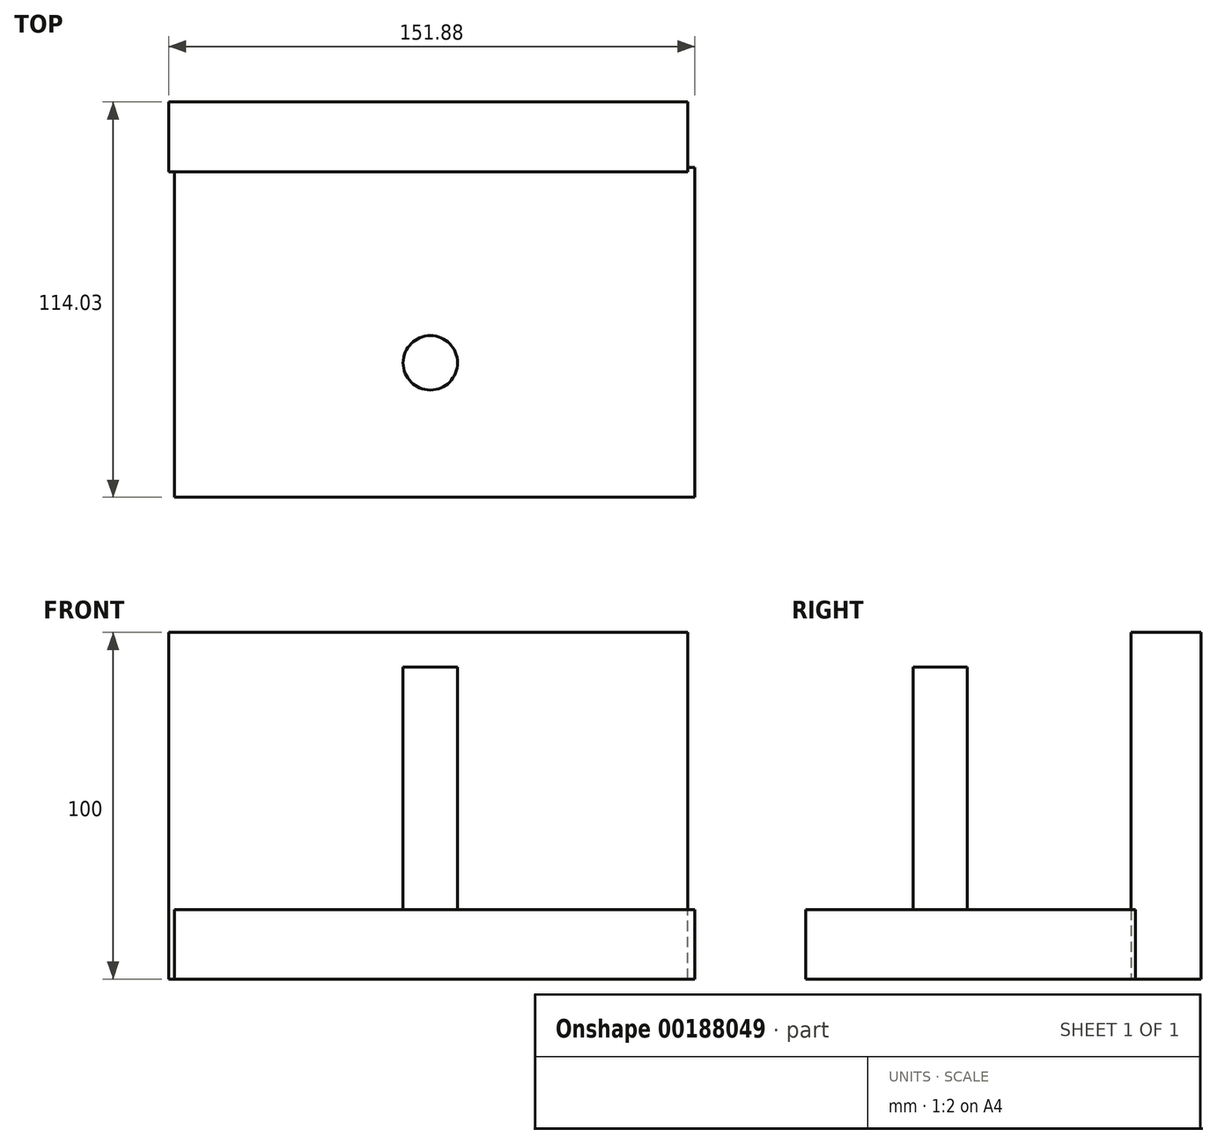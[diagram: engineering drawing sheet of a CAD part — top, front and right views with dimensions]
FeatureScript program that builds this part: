
annotation { "Feature Type Name" : "Feature", "Feature Type Description" : "" }
export const myFeature = defineFeature(function(context is Context, id is Id, definition is map)
    precondition{}
    {
        {
            var Q0;
            Q0=qCreatedBy(makeId("Top.planeOp"),FACE);
            var sketch = newSketch(context, id + "F0", { "sketchPlane" : qUnion([Q0])});
            skLineSegment(sketch, "E0", {"start": v(-73.83, -75.13) * mm, "end": v(76.36, -75.13) * mm});
            skLineSegment(sketch, "E1", {"start": v(-73.83, -75.13) * mm, "end": v(-73.83, 19.99) * mm});
            skLineSegment(sketch, "E2", {"start": v(-73.83, 19.99) * mm, "end": v(76.36, 19.99) * mm});
            skLineSegment(sketch, "E3", {"start": v(76.36, 19.99) * mm, "end": v(76.36, -75.13) * mm});
            skSolve(sketch);
        }
        {
            var Q0;
            Q0=makeQuery(id+"F0.imprint","IMPRINT",FACE,{"disambiguationData":[TD([[makeQuery(id+"F0.imprint","IMPRINT",EDGE,{"derivedFrom":sQuery(id+"F0.wireOp",EDGE,"E0")}),1.0]])]});
            extrude(context, id + "F1", {"entities" : qUnion([Q0]), "depth" : 20 * mm});
        }
        {
            var Q0;
            Q0=makeQuery(id+"F1.opExtrude","CAP_FACE",FACE,{"disambiguationData":[OSD([sQuery(id+"F0.wireOp",EDGE,"E0"),sQuery(id+"F0.wireOp",EDGE,"E1"),sQuery(id+"F0.wireOp",EDGE,"E2"),sQuery(id+"F0.wireOp",EDGE,"E3")])],"isStart":false});
            var sketch = newSketch(context, id + "F2", { "sketchPlane" : qUnion([Q0])});
            skCircle(sketch, "E4", {"center": v(0, -36.37) * mm, "radius": 7.84 * mm});
            skCircle(sketch, "E5", {"center": v(-30.7, -36.55) * mm, "radius": 4.32 * mm});
            skCircle(sketch, "E6", {"center": v(33.36, -36.92) * mm, "radius": 4.23 * mm});
            skSolve(sketch);
        }
        {
            var Q0;
            Q0=makeQuery(id+"F2.imprint","IMPRINT",FACE,{"disambiguationData":[TD([[makeQuery(id+"F2.imprint","IMPRINT",EDGE,{"derivedFrom":sQuery(id+"F2.wireOp",EDGE,"E4")}),1.0]])]});
            extrude(context, id + "F3", {"entities" : qUnion([Q0]), "operationType" : NewBodyOperationType.ADD, "depth" : 70 * mm});
        }
        {
            var Q0;
            Q0=qCreatedBy(makeId("Top.planeOp"),FACE);
            var sketch = newSketch(context, id + "F4", { "sketchPlane" : qUnion([Q0])});
            skLineSegment(sketch, "E7.bottom", {"start": v(-75.52, 18.7) * mm, "end": v(74.2, 18.7) * mm});
            skLineSegment(sketch, "E7.top", {"start": v(-75.52, 38.9) * mm, "end": v(74.2, 38.9) * mm});
            skLineSegment(sketch, "E7.left", {"start": v(-75.52, 18.7) * mm, "end": v(-75.52, 38.9) * mm});
            skLineSegment(sketch, "E7.right", {"start": v(74.2, 18.7) * mm, "end": v(74.2, 38.9) * mm});
            skSolve(sketch);
        }
        {
            var Q0;
            Q0=makeQuery(id+"F4.imprint","IMPRINT",FACE,{"disambiguationData":[TD([[makeQuery(id+"F4.imprint","IMPRINT",EDGE,{"derivedFrom":sQuery(id+"F4.wireOp",EDGE,"E7.bottom")}),1.0]])]});
            extrude(context, id + "F5", {"entities" : qUnion([Q0]), "operationType" : NewBodyOperationType.ADD, "depth" : 100 * mm});
        }
    });
